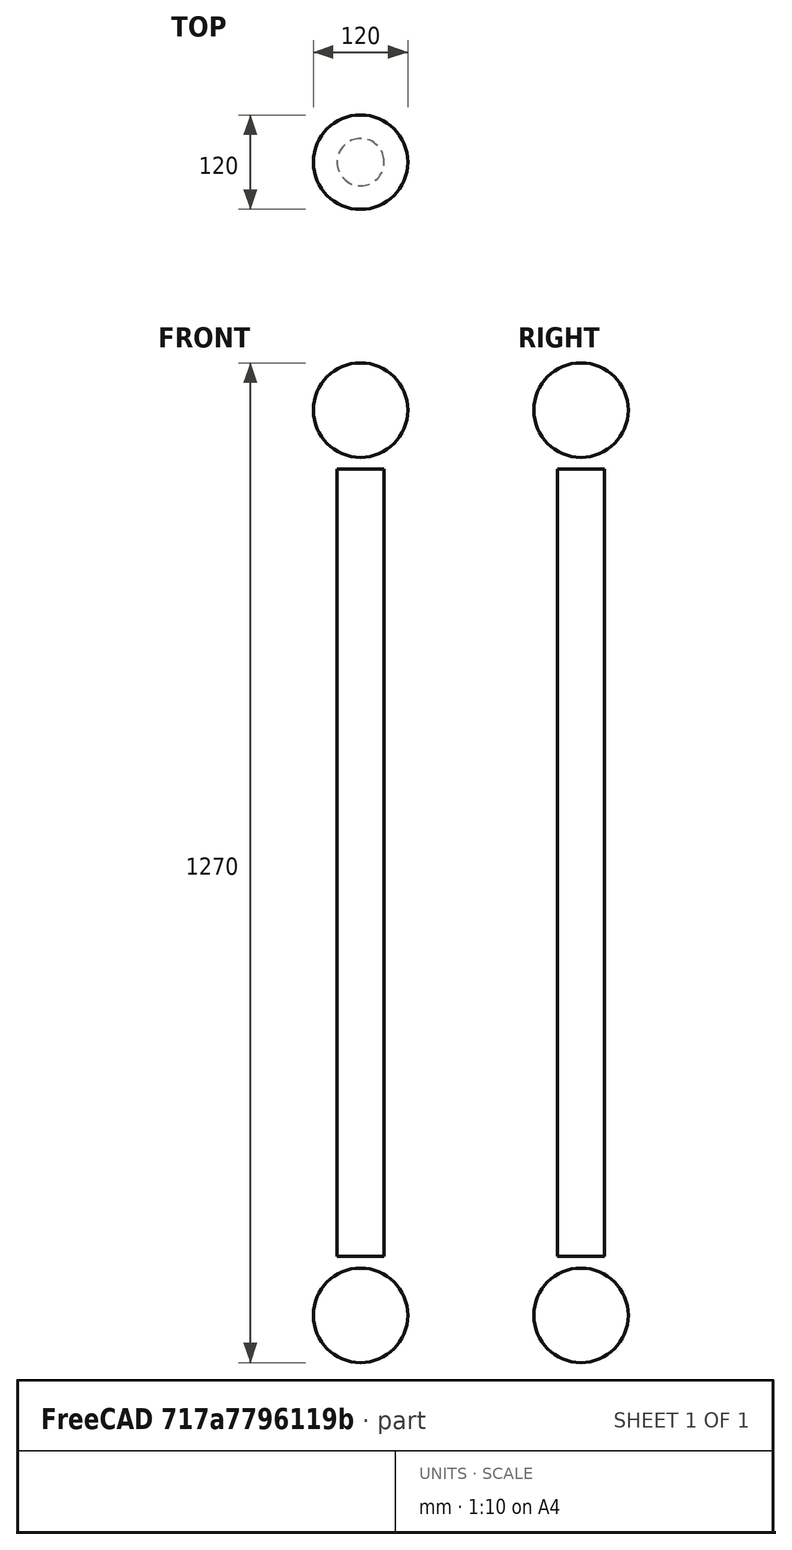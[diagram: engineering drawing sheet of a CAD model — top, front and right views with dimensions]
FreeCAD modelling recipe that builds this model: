
FCSTD DOCUMENT  (FreeCAD 1.0R39319 (Git))
Label: sp n cyl1
License: All rights reserved
LicenseURL: https://en.wikipedia.org/wiki/All_rights_reserved
objects: Part::Sphere×2, Part::Cylinder×1, Part::MultiFuse×1
note: 4 computed .brp shape members not serialized (recipe doc carries the construction recipe); baked Part::Feature solids carry a one-line shape summary decoded from their .brp

FEATURE [Part::Cylinder] cylinder
  Angle = 360
  AttacherType = Attacher::AttachEngine3D
  FirstAngle = 0
  Height = 1000
  Placement = pos=(0,0,-500) rot=(0,0,1;0rad)
  Radius = 30
  SecondAngle = 0
FEATURE [Part::Sphere] sphere
  Angle1 = -90
  Angle2 = 90
  Angle3 = 360
  AttacherType = Attacher::AttachEngine3D
  Placement = pos=(0,0,-575) rot=(0,0,1;0rad)
  Radius = 60
FEATURE [Part::Sphere] sphere001
  Angle1 = -90
  Angle2 = 90
  Angle3 = 360
  AttacherType = Attacher::AttachEngine3D
  Placement = pos=(0,0,575) rot=(0,0,1;0rad)
  Radius = 60
FEATURE [Part::MultiFuse] union
  Shapes = -> [cylinder,sphere,sphere001]
